FCSTD DOCUMENT  (FreeCAD 0.15R4671 (Git))
Label: te
License: All rights reserved
LicenseURL: http://en.wikipedia.org/wiki/All_rights_reserved
objects: Sketcher::SketchObject×1
note: 1 computed .brp shape members not serialized (recipe doc carries the construction recipe); baked Part::Feature solids carry a one-line shape summary decoded from their .brp

FEATURE [Sketcher::SketchObject] Sketch  label="Sechkant"
  sketch-geometry (6):
    g0: LineSegment StartX=-10 StartY=17.3205 StartZ=0 EndX=10 EndY=17.3205 EndZ=0
    g1: LineSegment StartX=10 StartY=17.3205 StartZ=0 EndX=20 EndY=0 EndZ=0
    g2: LineSegment StartX=20 StartY=0 StartZ=0 EndX=10 EndY=-17.3205 EndZ=0
    g3: LineSegment StartX=10 StartY=-17.3205 StartZ=0 EndX=-10 EndY=-17.3205 EndZ=0
    g4: LineSegment StartX=-10 StartY=-17.3205 StartZ=0 EndX=-20 EndY=3e-12 EndZ=0
    g5: LineSegment StartX=-20 StartY=3e-12 StartZ=0 EndX=-10 EndY=17.3205 EndZ=0
  constraints (18):
    c: Horizontal(g0)
    c: Coincident(g0,g1)
    c: PointOnObject(g1,g-1)
    c: Coincident(g1,g2)
    c: Coincident(g2,g3)
    c: Horizontal(g3)
    c: Coincident(g3,g4)
    c: Coincident(g4,g5)
    c: Coincident(g5,g0)
    c: Equal(g0,g1)
    c: Equal(g1,g2)
    c: Equal(g2,g3)
    c: Equal(g3,g4)
    c: Equal(g4,g5)
    c: Angle(g5,g0) = 2.0944
    c: Symmetric(g0,g0,g-2)
    c: DistanceX(g0) = 20
    c: Symmetric(g0,g2,g-1)
